FCSTD DOCUMENT  (FreeCAD 0.19R24267 +148 (Git))
Label: Tale
License: All rights reserved
LicenseURL: http://en.wikipedia.org/wiki/All_rights_reserved
objects: Sketcher::SketchObject×1, PartDesign::Body×1
note: 2 computed .brp shape members not serialized (recipe doc carries the construction recipe); baked Part::Feature solids carry a one-line shape summary decoded from their .brp

FEATURE [Sketcher::SketchObject] Sketch
  FullyConstrained = false
  MapMode = 5
  Support = -> [XY_Plane]
  sketch-geometry (16):
    g0: LineSegment StartX=-40 StartY=18 StartZ=0 EndX=40 EndY=18 EndZ=0
    g1: LineSegment StartX=40 StartY=-18 StartZ=0 EndX=-40 EndY=-18 EndZ=0
    g2: ArcOfCircle CenterX=-40 CenterY=-4.82e-14 CenterZ=0 NormalX=0 NormalY=0 NormalZ=1 AngleXU=0 Radius=18 StartAngle=1.5708 EndAngle=4.71239
    g3: ArcOfCircle CenterX=40 CenterY=-4.71e-14 CenterZ=0 NormalX=0 NormalY=0 NormalZ=1 AngleXU=0 Radius=18 StartAngle=4.71239 EndAngle=7.85398
    g4: LineSegment StartX=22.5 StartY=-18 StartZ=0 EndX=-22.5 EndY=-18 EndZ=0
    g5: LineSegment StartX=-22.5 StartY=-18 StartZ=0 EndX=-22.5 EndY=18 EndZ=0
    g6: LineSegment StartX=-22.5 StartY=18 StartZ=0 EndX=22.5 EndY=18 EndZ=0
    g7: LineSegment StartX=22.5 StartY=18 StartZ=0 EndX=22.5 EndY=-18 EndZ=0
    g8: Circle CenterX=-40 CenterY=-4.82e-14 CenterZ=0 NormalX=0 NormalY=0 NormalZ=1 AngleXU=0 Radius=10
    g9: Circle CenterX=40 CenterY=-4.71e-14 CenterZ=0 NormalX=0 NormalY=0 NormalZ=1 AngleXU=0 Radius=10
    g10: Circle CenterX=40 CenterY=-4.71e-14 CenterZ=0 NormalX=0 NormalY=0 NormalZ=1 AngleXU=0 Radius=5.5
    g11: Circle CenterX=-40 CenterY=-4.82e-14 CenterZ=0 NormalX=0 NormalY=0 NormalZ=1 AngleXU=0 Radius=5.5
    g12: LineSegment StartX=-18 StartY=14 StartZ=0 EndX=18 EndY=14 EndZ=0
    g13: LineSegment StartX=18 StartY=14 StartZ=0 EndX=18 EndY=-14 EndZ=0
    g14: LineSegment StartX=18 StartY=-14 StartZ=0 EndX=-18 EndY=-14 EndZ=0
    g15: LineSegment StartX=-18 StartY=-14 StartZ=0 EndX=-18 EndY=14 EndZ=0
  constraints (39):
    c: Horizontal(g0)
    c: Horizontal(g1)
    c: Symmetric(g0,g1,g-1)
    c: DistanceX(g0,g0) = 80
    c: Coincident(g4,g5)
    c: Coincident(g5,g6)
    c: Coincident(g6,g7)
    c: Coincident(g7,g4)
    c: Horizontal(g4)
    c: Horizontal(g6)
    c: Vertical(g5)
    c: Vertical(g7)
    c: PointOnObject(g4,g1)
    c: DistanceX(g5,g6) = 45
    c: Tangent(g2,g0) = 1.5708
    c: Symmetric(g5,g4,g-1)
    c: Coincident(g8,g2)
    c: Coincident(g9,g3)
    c: Coincident(g10,g3)
    c: Coincident(g11,g2)
    c: Diameter(g9) = 20
    c: Diameter(g10) = 11
    c: Diameter(g11) = 11
    c: Diameter(g8) = 20
    c: Tangent(g3,g0) = 1.5708
    c: Tangent(g1,g3)
    c: Tangent(g2,g1) = 1.5708
    c: Radius(g3) = 18
    c: Coincident(g12,g13)
    c: Coincident(g13,g14)
    c: Coincident(g14,g15)
    c: Coincident(g15,g12)
    c: Horizontal(g12)
    c: Horizontal(g14)
    c: Vertical(g13)
    c: Vertical(g15)
    c: Symmetric(g13,g12,g-1)
    c: DistanceY(g14,g12) = 28
    c: DistanceX(g12,g12) = 36
FEATURE [PartDesign::Body] Body
  Group = -> [Sketch]
  Origin = -> Origin
